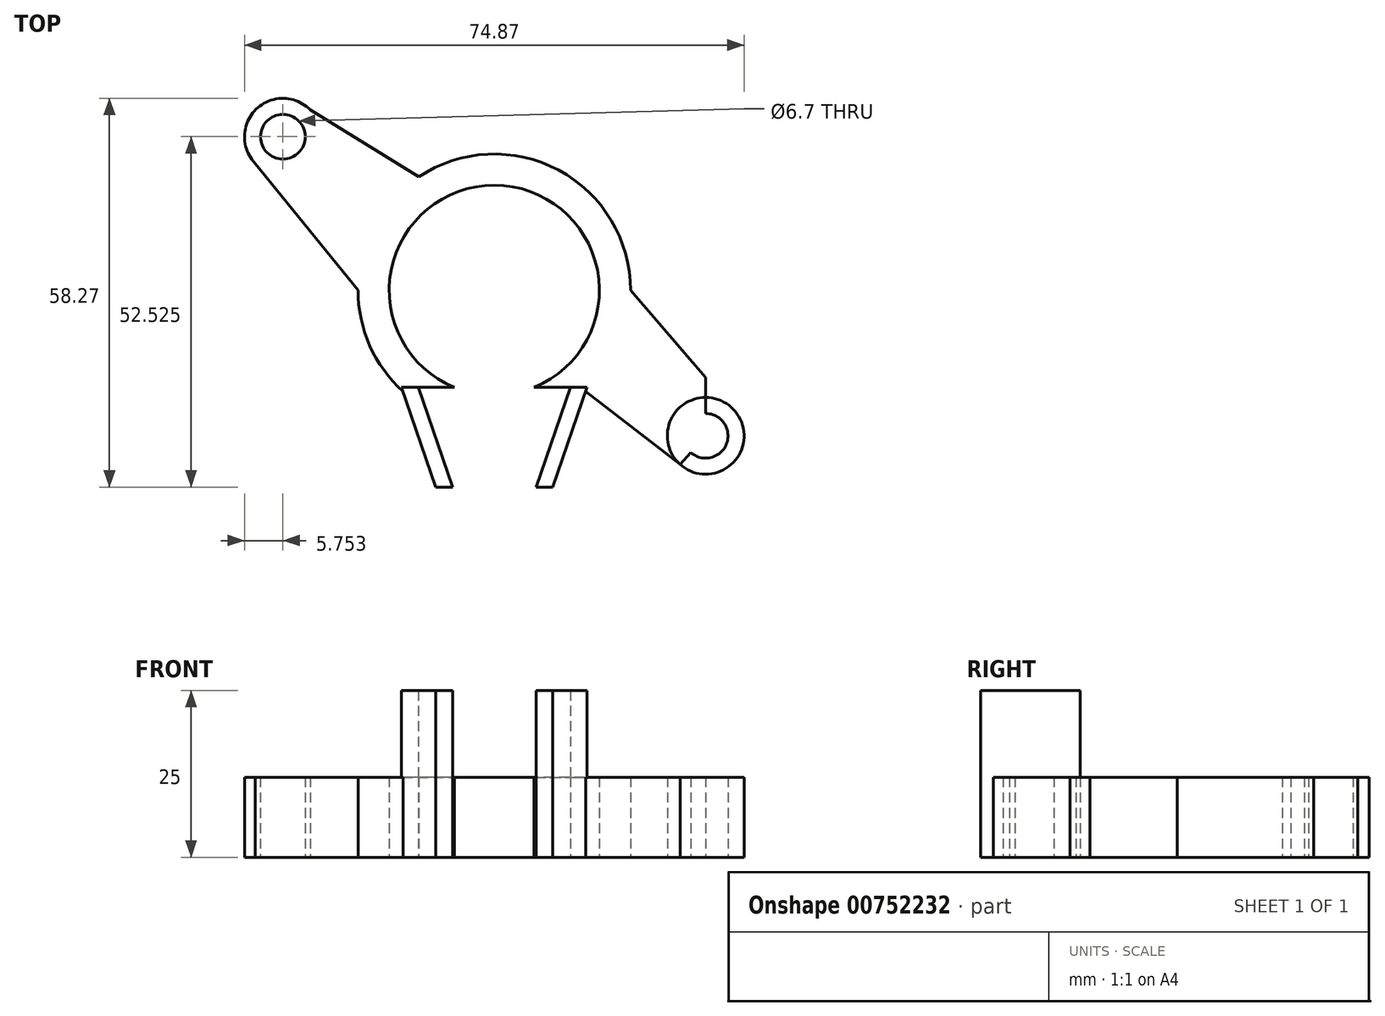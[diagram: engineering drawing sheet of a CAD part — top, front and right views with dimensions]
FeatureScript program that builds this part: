
annotation { "Feature Type Name" : "Feature", "Feature Type Description" : "" }
export const myFeature = defineFeature(function(context is Context, id is Id, definition is map)
    precondition{}
    {
        {
            var Q0;
            Q0=qCreatedBy(makeId("Top.planeOp"),FACE);
            var sketch = newSketch(context, id + "F0", { "sketchPlane" : qUnion([Q0])});
            skLineSegment(sketch, "E0.bottom", {"start": v(-52.47, 38.18) * mm, "end": v(4.2, 38.18) * mm});
            skLineSegment(sketch, "E0.left", {"start": v(-55.82, 34.83) * mm, "end": v(-55.82, -4.47) * mm});
            skLineSegment(sketch, "E0.right", {"start": v(7.55, 34.83) * mm, "end": v(7.55, -3.3) * mm});
            skCircle(sketch, "E1", {"center": v(7.55, 38.18) * mm, "radius": 3.35 * mm});
            skCircle(sketch, "E2", {"center": v(-55.82, 38.18) * mm, "radius": 3.35 * mm});
            skCircle(sketch, "E3", {"center": v(-55.82, -7.82) * mm, "radius": 3.35 * mm});
            skCircle(sketch, "E4", {"center": v(7.55, -6.66) * mm, "radius": 3.35 * mm});
            skCircle(sketch, "E5", {"center": v(-55.82, 38.18) * mm, "radius": 5.75 * mm});
            skCircle(sketch, "E6", {"center": v(7.55, 38.18) * mm, "radius": 5.75 * mm});
            skCircle(sketch, "E7", {"center": v(7.55, -6.66) * mm, "radius": 5.75 * mm});
            skCircle(sketch, "E8", {"center": v(-55.82, -7.82) * mm, "radius": 5.75 * mm});
            skPoint(sketch, "E9.first.point", {"position": v(-24.13, 38.18) * mm});
            skPoint(sketch, "E9.second.point", {"position": v(-55.82, 15.18) * mm});
            skPoint(sketch, "E10.middle", {"position": v(-24.13, 15.17) * mm});
            skCircle(sketch, "E11", {"center": v(-24.13, 15.17) * mm, "radius": 15.75 * mm});
            skLineSegment(sketch, "E12", {"start": v(-24.13, -7.82) * mm, "end": v(-24.13, -7.85) * mm});
            skLineSegment(sketch, "E13", {"start": v(-35.53, 0.6) * mm, "end": v(-30.38, -14.34) * mm});
            skLineSegment(sketch, "E14", {"start": v(-17.88, -14.34) * mm, "end": v(-12.74, 0.6) * mm});
            skLineSegment(sketch, "E15", {"start": v(-30.38, -14.34) * mm, "end": v(-32.88, -14.34) * mm});
            skLineSegment(sketch, "E16", {"start": v(-32.88, -14.34) * mm, "end": v(-38.03, 0.64) * mm});
            skLineSegment(sketch, "E17", {"start": v(-38.03, 0.64) * mm, "end": v(-35.53, 0.6) * mm});
            skLineSegment(sketch, "E18", {"start": v(-17.88, -14.34) * mm, "end": v(-15.38, -14.34) * mm});
            skLineSegment(sketch, "E19", {"start": v(-15.38, -14.34) * mm, "end": v(-10.24, 0.6) * mm});
            skLineSegment(sketch, "E20", {"start": v(-10.24, 0.6) * mm, "end": v(-12.74, 0.6) * mm});
            skLineSegment(sketch, "E21.trimOffspring", {"start": v(-55.82, -7.82) * mm, "end": v(-55.82, -7.85) * mm});
            skLineSegment(sketch, "E22.trimOffspring", {"start": v(7.55, 38.18) * mm, "end": v(7.55, 38.18) * mm});
            skPoint(sketch, "E23.orphan", {"position": v(-24.13, -14.34) * mm});
            skLineSegment(sketch, "E24", {"start": v(-24.13, 15.17) * mm, "end": v(-42.63, 15.17) * mm});
            skLineSegment(sketch, "E25", {"start": v(-35.53, 0.6) * mm, "end": v(-42.63, 15.17) * mm});
            skLineSegment(sketch, "E26", {"start": v(-24.13, 15.17) * mm, "end": v(-5.63, 15.17) * mm});
            skLineSegment(sketch, "E27", {"start": v(-12.74, 0.6) * mm, "end": v(-5.63, 15.17) * mm});
            skLineSegment(sketch, "E28", {"start": v(-30.38, -14.34) * mm, "end": v(-17.88, -14.34) * mm});
            skLineSegment(sketch, "E29", {"start": v(-42.63, 15.17) * mm, "end": v(-55.82, 15.18) * mm});
            skLineSegment(sketch, "E30", {"start": v(-5.63, 15.17) * mm, "end": v(7.55, 15.17) * mm});
            skLineSegment(sketch, "E31", {"start": v(-24.13, 15.17) * mm, "end": v(-24.13, -14.34) * mm});
            skLineSegment(sketch, "E32", {"start": v(-24.13, 15.17) * mm, "end": v(-24.13, 38.18) * mm});
            skLineSegment(sketch, "E33", {"start": v(-35.53, 0.6) * mm, "end": v(-12.74, 0.6) * mm});
            skLineSegment(sketch, "E34", {"start": v(-24.13, -7.82) * mm, "end": v(1.92, -7.82) * mm});
            skLineSegment(sketch, "E35", {"start": v(-24.13, -7.82) * mm, "end": v(-50.07, -7.82) * mm});
            skLineSegment(sketch, "E36", {"start": v(7.55, -6.66) * mm, "end": v(11.38, -2.37) * mm});
            skLineSegment(sketch, "E37", {"start": v(11.38, -2.37) * mm, "end": v(7.55, -6.66) * mm});
            skLineSegment(sketch, "E38", {"start": v(7.55, -6.66) * mm, "end": v(3.72, -10.95) * mm});
            skLineSegment(sketch, "E39", {"start": v(-55.82, 38.18) * mm, "end": v(-59.94, 34.18) * mm});
            skLineSegment(sketch, "E40", {"start": v(-55.82, 38.18) * mm, "end": v(-51.7, 42.2) * mm});
            skArc(sketch, "E41", {"start": v(-3.71, 15.17) * mm, "mid": v(-32.43, 33.82) * mm, "end": v(-37.8, 0) * mm});
            skLineSegment(sketch, "E42", {"start": v(11.38, -2.37) * mm, "end": v(-3.71, 15.17) * mm});
            skLineSegment(sketch, "E43", {"start": v(-51.7, 42.2) * mm, "end": v(-35.46, 32.16) * mm});
            skLineSegment(sketch, "E44", {"start": v(-59.94, 34.18) * mm, "end": v(-44.55, 15.17) * mm});
            skPoint(sketch, "E45.trimOffspring.end.orphan", {"position": v(-10.24, 0.2) * mm});
            skLineSegment(sketch, "E46", {"start": v(3.72, -10.95) * mm, "end": v(-10.44, 0) * mm});
            skSolve(sketch);
        }
        {
            var Q0;
            {var subQ7=sQuery(id+"F0.wireOp",EDGE,"E5");var subQ9=sQuery(id+"F0.wireOp",EDGE,"E0.bottom");var subQ11=makeQuery(id+"F0.imprint","INTERSECT",VERTEX,{"derivedFrom":[subQ7,subQ9]});Q0=makeQuery(id+"F0.imprint","IMPRINT",FACE,{"disambiguationData":[TD([[makeQuery(id+"F0.imprint","IMPRINT",EDGE,{"disambiguationData":[TD([[subQ11,1.0]])],"derivedFrom":subQ7}),-1.0]])]});}
            var Q1;
            {var subQ0=sQuery(id+"F0.wireOp",EDGE,"E32");var subQ1=sQuery(id+"F0.wireOp",EDGE,"E11");var subQ2=makeQuery(id+"F0.imprint","INTERSECT",VERTEX,{"derivedFrom":[subQ1,subQ0]});Q1=makeQuery(id+"F0.imprint","IMPRINT",FACE,{"disambiguationData":[TD([[makeQuery(id+"F0.imprint","IMPRINT",EDGE,{"disambiguationData":[TD([[subQ2,-1.0]])],"derivedFrom":subQ1}),-1.0]])]});}
            var Q2;
            {var subQ0=sQuery(id+"F0.wireOp",EDGE,"E32");var subQ1=sQuery(id+"F0.wireOp",EDGE,"E11");var subQ2=makeQuery(id+"F0.imprint","INTERSECT",VERTEX,{"derivedFrom":[subQ1,subQ0]});Q2=makeQuery(id+"F0.imprint","IMPRINT",FACE,{"disambiguationData":[TD([[makeQuery(id+"F0.imprint","IMPRINT",EDGE,{"disambiguationData":[TD([[subQ2,1.0]])],"derivedFrom":subQ1}),-1.0]])]});}
            var Q3;
            {var subQ0=sQuery(id+"F0.wireOp",EDGE,"E20");Q3=makeQuery(id+"F0.imprint","IMPRINT",FACE,{"disambiguationData":[TD([[makeQuery(id+"F0.imprint","IMPRINT",EDGE,{"derivedFrom":subQ0}),-1.0]])]});}
            var Q4;
            {var subQ0=sQuery(id+"F0.wireOp",EDGE,"E20");Q4=makeQuery(id+"F0.imprint","IMPRINT",FACE,{"disambiguationData":[TD([[makeQuery(id+"F0.imprint","IMPRINT",EDGE,{"derivedFrom":subQ0}),1.0]])]});}
            var Q5;
            {var subQ0=sQuery(id+"F0.wireOp",EDGE,"E18");Q5=makeQuery(id+"F0.imprint","IMPRINT",FACE,{"disambiguationData":[TD([[makeQuery(id+"F0.imprint","IMPRINT",EDGE,{"derivedFrom":subQ0}),1.0]])]});}
            var Q6;
            {var subQ0=sQuery(id+"F0.wireOp",EDGE,"E31");var subQ3=makeQuery(id+"F0.imprint","IMPRINT",VERTEX,{"derivedFrom":subQ0});Q6=makeQuery(id+"F0.imprint","IMPRINT",FACE,{"disambiguationData":[TD([[makeQuery(id+"F0.imprint","IMPRINT",EDGE,{"disambiguationData":[TD([[subQ3,-1.0]])],"derivedFrom":subQ0}),1.0]])]});}
            var Q7;
            {var subQ0=sQuery(id+"F0.wireOp",EDGE,"E15");Q7=makeQuery(id+"F0.imprint","IMPRINT",FACE,{"disambiguationData":[TD([[makeQuery(id+"F0.imprint","IMPRINT",EDGE,{"derivedFrom":subQ0}),-1.0]])]});}
            var Q8;
            {var subQ0=sQuery(id+"F0.wireOp",EDGE,"E17");Q8=makeQuery(id+"F0.imprint","IMPRINT",FACE,{"disambiguationData":[TD([[makeQuery(id+"F0.imprint","IMPRINT",EDGE,{"derivedFrom":subQ0}),-1.0]])]});}
            var Q9;
            {var subQ1=sQuery(id+"F0.wireOp",EDGE,"E17");Q9=makeQuery(id+"F0.imprint","IMPRINT",FACE,{"disambiguationData":[TD([[makeQuery(id+"F0.imprint","IMPRINT",EDGE,{"derivedFrom":subQ1}),1.0]])]});}
            var Q10;
            {var subQ0=sQuery(id+"F0.wireOp",EDGE,"E0.right");var subQ1=sQuery(id+"F0.wireOp",EDGE,"E4");var subQ2=makeQuery(id+"F0.imprint","INTERSECT",VERTEX,{"derivedFrom":[subQ1,subQ0]});Q10=makeQuery(id+"F0.imprint","IMPRINT",FACE,{"disambiguationData":[TD([[makeQuery(id+"F0.imprint","IMPRINT",EDGE,{"disambiguationData":[TD([[subQ2,1.0]])],"derivedFrom":subQ1}),-1.0]])]});}
            var Q11;
            {var subQ0=sQuery(id+"F0.wireOp",EDGE,"E0.right");var subQ1=sQuery(id+"F0.wireOp",EDGE,"E4");var subQ2=makeQuery(id+"F0.imprint","INTERSECT",VERTEX,{"derivedFrom":[subQ1,subQ0]});Q11=makeQuery(id+"F0.imprint","IMPRINT",FACE,{"disambiguationData":[TD([[makeQuery(id+"F0.imprint","IMPRINT",EDGE,{"disambiguationData":[TD([[subQ2,-1.0]])],"derivedFrom":subQ1}),-1.0]])]});}
            var Q12;
            {var subQ0=sQuery(id+"F0.wireOp",EDGE,"E37");var subQ1=sQuery(id+"F0.wireOp",EDGE,"E4");var subQ2=makeQuery(id+"F0.imprint","INTERSECT",VERTEX,{"derivedFrom":[subQ1,subQ0]});Q12=makeQuery(id+"F0.imprint","IMPRINT",FACE,{"disambiguationData":[TD([[makeQuery(id+"F0.imprint","IMPRINT",EDGE,{"disambiguationData":[TD([[subQ2,1.0]])],"derivedFrom":subQ1}),-1.0]])]});}
            var Q13;
            {var subQ0=sQuery(id+"F0.wireOp",EDGE,"E42");var subQ3=sQuery(id+"F0.wireOp",EDGE,"E0.right");var subQ5=makeQuery(id+"F0.imprint","INTERSECT",VERTEX,{"derivedFrom":[subQ3,subQ0]});Q13=makeQuery(id+"F0.imprint","IMPRINT",FACE,{"disambiguationData":[TD([[makeQuery(id+"F0.imprint","IMPRINT",EDGE,{"disambiguationData":[TD([[subQ5,-1.0]])],"derivedFrom":subQ3}),1.0]])]});}
            var Q14;
            {var subQ0=sQuery(id+"F0.wireOp",EDGE,"E44");var subQ3=sQuery(id+"F0.wireOp",EDGE,"E0.left");var subQ5=makeQuery(id+"F0.imprint","INTERSECT",VERTEX,{"derivedFrom":[subQ3,subQ0]});Q14=makeQuery(id+"F0.imprint","IMPRINT",FACE,{"disambiguationData":[TD([[makeQuery(id+"F0.imprint","IMPRINT",EDGE,{"disambiguationData":[TD([[subQ5,1.0]])],"derivedFrom":subQ3}),-1.0]])]});}
            var Q15;
            {var subQ0=sQuery(id+"F0.wireOp",EDGE,"E0.bottom");var subQ1=sQuery(id+"F0.wireOp",EDGE,"E2");var subQ2=makeQuery(id+"F0.imprint","INTERSECT",VERTEX,{"derivedFrom":[subQ1,subQ0]});Q15=makeQuery(id+"F0.imprint","IMPRINT",FACE,{"disambiguationData":[TD([[makeQuery(id+"F0.imprint","IMPRINT",EDGE,{"disambiguationData":[TD([[subQ2,1.0]])],"derivedFrom":subQ1}),-1.0]])]});}
            var Q16;
            {var subQ0=sQuery(id+"F0.wireOp",EDGE,"E0.left");var subQ1=sQuery(id+"F0.wireOp",EDGE,"E2");var subQ2=makeQuery(id+"F0.imprint","INTERSECT",VERTEX,{"derivedFrom":[subQ1,subQ0]});Q16=makeQuery(id+"F0.imprint","IMPRINT",FACE,{"disambiguationData":[TD([[makeQuery(id+"F0.imprint","IMPRINT",EDGE,{"disambiguationData":[TD([[subQ2,1.0]])],"derivedFrom":subQ1}),-1.0]])]});}
            var Q17;
            {var subQ0=sQuery(id+"F0.wireOp",EDGE,"E40");var subQ1=sQuery(id+"F0.wireOp",EDGE,"E2");var subQ2=makeQuery(id+"F0.imprint","INTERSECT",VERTEX,{"derivedFrom":[subQ1,subQ0]});Q17=makeQuery(id+"F0.imprint","IMPRINT",FACE,{"disambiguationData":[TD([[makeQuery(id+"F0.imprint","IMPRINT",EDGE,{"disambiguationData":[TD([[subQ2,-1.0]])],"derivedFrom":subQ1}),-1.0]])]});}
            var Q18;
            {var subQ0=sQuery(id+"F0.wireOp",EDGE,"E0.bottom");var subQ1=sQuery(id+"F0.wireOp",EDGE,"E2");var subQ2=makeQuery(id+"F0.imprint","INTERSECT",VERTEX,{"derivedFrom":[subQ1,subQ0]});Q18=makeQuery(id+"F0.imprint","IMPRINT",FACE,{"disambiguationData":[TD([[makeQuery(id+"F0.imprint","IMPRINT",EDGE,{"disambiguationData":[TD([[subQ2,-1.0]])],"derivedFrom":subQ1}),-1.0]])]});}
            var Q19;
            {var subQ0=sQuery(id+"F0.wireOp",EDGE,"E43");var subQ3=sQuery(id+"F0.wireOp",EDGE,"E0.bottom");var subQ5=makeQuery(id+"F0.imprint","INTERSECT",VERTEX,{"derivedFrom":[subQ3,subQ0]});Q19=makeQuery(id+"F0.imprint","IMPRINT",FACE,{"disambiguationData":[TD([[makeQuery(id+"F0.imprint","IMPRINT",EDGE,{"disambiguationData":[TD([[subQ5,1.0]])],"derivedFrom":subQ3}),1.0]])]});}
            var Q20;
            {var subQ1=sQuery(id+"F0.wireOp",EDGE,"E31");var subQ3=makeQuery(id+"F0.imprint","IMPRINT",VERTEX,{"derivedFrom":subQ1});Q20=makeQuery(id+"F0.imprint","IMPRINT",FACE,{"disambiguationData":[TD([[makeQuery(id+"F0.imprint","IMPRINT",EDGE,{"disambiguationData":[TD([[subQ3,-1.0]])],"derivedFrom":subQ1}),-1.0]])]});}
            var Q21;
            {var subQ5=sQuery(id+"F0.wireOp",EDGE,"E25");Q21=makeQuery(id+"F0.imprint","IMPRINT",FACE,{"disambiguationData":[TD([[makeQuery(id+"F0.imprint","IMPRINT",EDGE,{"derivedFrom":subQ5}),-1.0]])]});}
            var Q22;
            {var subQ5=sQuery(id+"F0.wireOp",EDGE,"E27");Q22=makeQuery(id+"F0.imprint","IMPRINT",FACE,{"disambiguationData":[TD([[makeQuery(id+"F0.imprint","IMPRINT",EDGE,{"derivedFrom":subQ5}),1.0]])]});}
            extrude(context, id + "F1", {"entities" : qUnion([Q0, Q1, Q2, Q3, Q4, Q5, Q6, Q7, Q8, Q9, Q10, Q11, Q12, Q13, Q14, Q15, Q16, Q17, Q18, Q19, Q20, Q21, Q22]), "depth" : 12 * mm, "offsetDistance" : 25 * mm});
        }
        {
            var Q0;
            {var subQ0=sQuery(id+"F0.wireOp",EDGE,"E17");Q0=makeQuery(id+"F0.imprint","IMPRINT",FACE,{"disambiguationData":[TD([[makeQuery(id+"F0.imprint","IMPRINT",EDGE,{"derivedFrom":subQ0}),-1.0]])]});}
            var Q1;
            {var subQ0=sQuery(id+"F0.wireOp",EDGE,"E15");Q1=makeQuery(id+"F0.imprint","IMPRINT",FACE,{"disambiguationData":[TD([[makeQuery(id+"F0.imprint","IMPRINT",EDGE,{"derivedFrom":subQ0}),-1.0]])]});}
            var Q2;
            {var subQ0=sQuery(id+"F0.wireOp",EDGE,"E18");Q2=makeQuery(id+"F0.imprint","IMPRINT",FACE,{"disambiguationData":[TD([[makeQuery(id+"F0.imprint","IMPRINT",EDGE,{"derivedFrom":subQ0}),1.0]])]});}
            var Q3;
            {var subQ0=sQuery(id+"F0.wireOp",EDGE,"E20");Q3=makeQuery(id+"F0.imprint","IMPRINT",FACE,{"disambiguationData":[TD([[makeQuery(id+"F0.imprint","IMPRINT",EDGE,{"derivedFrom":subQ0}),1.0]])]});}
            extrude(context, id + "F2", {"entities" : qUnion([Q0, Q1, Q2, Q3]), "operationType" : NewBodyOperationType.ADD, "depth" : 25 * mm, "offsetDistance" : 25 * mm});
        }
        {
            var Q0;
            {var subQ0=sQuery(id+"F0.wireOp",EDGE,"E34");var subQ1=sQuery(id+"F0.wireOp",EDGE,"E7");var subQ2=makeQuery(id+"F0.imprint","INTERSECT",VERTEX,{"derivedFrom":[subQ1,subQ0]});Q0=makeQuery(id+"F0.imprint","IMPRINT",FACE,{"disambiguationData":[TD([[makeQuery(id+"F0.imprint","IMPRINT",EDGE,{"disambiguationData":[TD([[subQ2,1.0]])],"derivedFrom":subQ0}),-1.0]])]});}
            extrude(context, id + "F3", {"entities" : qUnion([Q0]), "operationType" : NewBodyOperationType.ADD, "depth" : 12 * mm, "offsetDistance" : 25 * mm});
        }
    });
